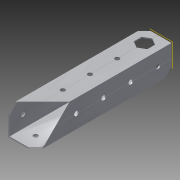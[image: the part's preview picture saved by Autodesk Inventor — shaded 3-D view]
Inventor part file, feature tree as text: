
AUTODESK INVENTOR PART (.ipt)
format: ipt  version: 2014 (Build 180170000, 170)  size: 1,250,816 bytes
history: native  units: in
note: dims shown in document units (in); Inventor stores cm internally (conversion verified against a paired STEP export)
features: extrude x2, sketch x2, pattern_circular x1, other x1, plane x1, imported_body x1
ambient origin geometry x8: Origin, YZ Plane, XZ Plane, XY Plane, X Axis, Y Axis, Z Axis, Center Point
bodies: Body1 (feature_tree)
feature tree (8):
  pattern_circular  "CirPattern2"
  other  "217-3426-STEP1"
  plane  "Work Plane1"
  extrude  "Extrusion1"  Depth=393.7008in TaperAngle=0.0deg
  extrude  "Extrusion5"  Depth=0.5in
  imported_body  "Base1"
  sketch  "Sketch1"  dims[d0=-7.0in d1=393.7008in d2=0.0in]
  sketch  "Sketch5"  dims[d21=3.937in d22=0.0in d23=0.5in d24=2.5in]
